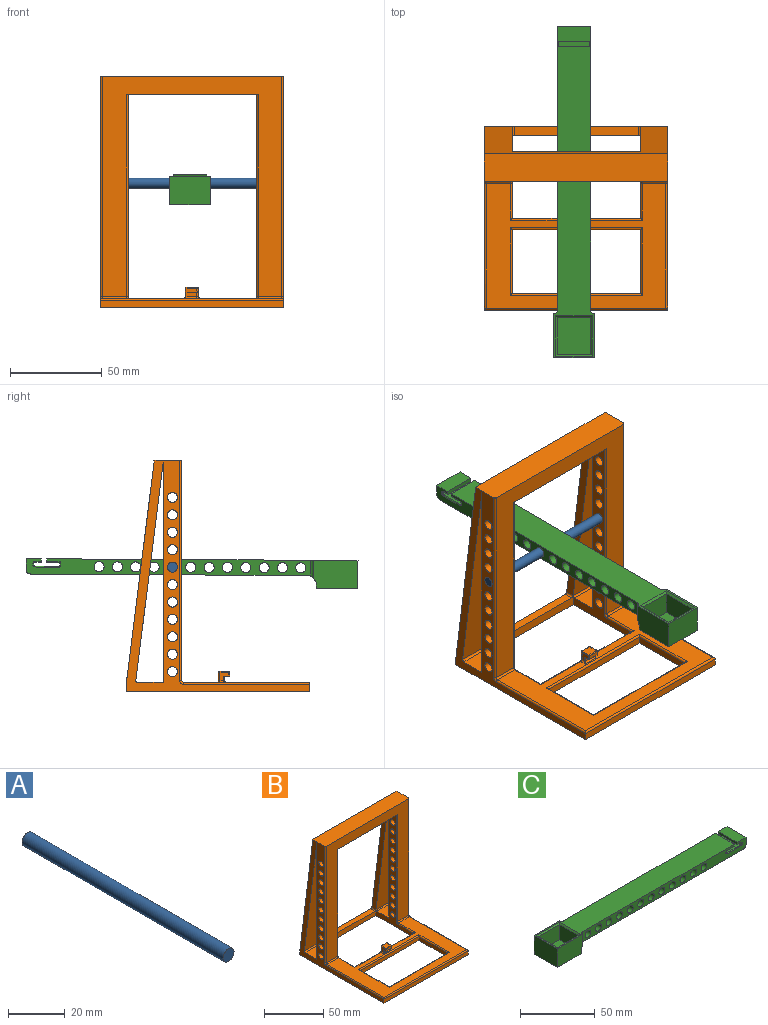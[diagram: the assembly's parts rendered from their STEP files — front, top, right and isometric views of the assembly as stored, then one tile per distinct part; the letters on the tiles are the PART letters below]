
ASSEMBLY  parts=3 mates=2
PART A: 3 faces, bbox 5.5x100x5.5 mm
  f0: cylinder r=2.75mm len=100mm, axis (0,1,0), area 1727.9mm2, adj f1,f2
  f1: plane 5.5x5.5mm, normal (0,-1,0), area 23.8mm2, adj f0
  f2: plane 5.5x5.5mm, normal (0,1,0), area 23.8mm2, adj f0
PART B: 108 faces, bbox 100.1x100.1x126.1 mm
  f0: plane 1.05x1.05mm, normal (0,-0.99,-0.12), area 0.2mm2, adj f25,f34,f106
  f1: plane 118.88x100mm, normal (0,-0.99,-0.12), area 4222.1mm2, adj f12,f13,f14,f22,f23,f24,f105,f107
  f2: plane 100x100mm, normal (0,0,-1), area 4421mm2, adj f7,f12,f13,f18,f19,f25,f27,f30
  f3: plane 98x67.9mm, normal (0,0,1), area 2547.8mm2, adj f60,f61,f67,f68,f70,f72,f73,f75
  f4: plane 14.67x13.96mm, normal (0,0,1), area 204.8mm2, adj f12,f14,f25,f107
  f5: plane 15.33x13.96mm, normal (0,0,1), area 214mm2, adj f13,f14,f27,f105
  f6: plane 68x5mm, normal (0,0,1), area 340mm2, adj f19,f34,f102,f106
  f7: plane 70x10.5mm, normal (0,1,0), area 316.6mm2, adj f2,f25,f27,f59,f60,f64,f74,f77
  f8: plane 5.87x5.25mm, normal (0,0,1), area 30.8mm2, adj f57,f92,f94,f95,f96
  f9: plane 5.87x2.16mm, normal (0,-1,0), area 12.6mm2, adj f58,f90,f92,f100
  f10: plane 6.34x3.14mm, normal (0,0,-1), area 17.7mm2, adj f11,f63,f98,f99,f100,f103
  f11: plane 5.87x2.32mm, normal (0,-1,0), area 13.6mm2, adj f10,f66,f72,f103
  f12: plane 126.06x100mm, normal (1,0,0), area 1863.8mm2, adj f1,f2,f4,f14,f17,f18,f19,f20
  f13: plane 126.06x100mm, normal (-1,0,0), area 1863.8mm2, adj f1,f2,f5,f14,f17,f18,f19,f20
  f14: plane 120x100mm, normal (0,1,0), area 4222.8mm2, adj f1,f4,f5,f12,f13,f25,f26,f27
  f15: plane 1.05x1.05mm, normal (0,-0.99,-0.12), area 0.2mm2, adj f27,f34,f102
  f16: plane 120.06x98mm, normal (0,-1,0), area 3838.7mm2, adj f21,f26,f62,f68,f69,f79,f83,f85
  f17: plane 120.05x100.05mm, normal (0,0.99,0.12), area 4256.6mm2, adj f12,f13,f19,f20,f22,f23,f24,f102
  f18: plane 100x4mm, normal (0,-1,0), area 400mm2, adj f2,f12,f13,f76
  f19: plane 100x5mm, normal (0,1,0), area 500mm2, adj f2,f6,f12,f13,f17
  f20: plane 100x1.06mm, normal (0,1,-0.06), area 106.3mm2, adj f12,f13,f17,f21
  f21: plane 100x15.06mm, normal (0,0,1), area 1505.7mm2, adj f12,f13,f16,f20,f69,f79
  f22: plane 110.1x18.85mm, normal (1,0,0), area 550.5mm2, adj f1,f17,f23,f27,f102
  f23: plane 70x5mm, normal (0,0,-1), area 350mm2, adj f1,f17,f22,f24
  f24: plane 110.1x18.85mm, normal (-1,0,0), area 550.5mm2, adj f1,f17,f23,f25,f106
  f25: plane 116.1x45mm, normal (-1,0,0), area 943.8mm2, adj f0,f2,f4,f7,f14,f24,f26,f34
  f26: plane 72x10mm, normal (0,0,-1), area 700.4mm2, adj f14,f16,f25,f27,f62,f85
  f27: plane 116.1x45mm, normal (1,0,0), area 943.8mm2, adj f2,f5,f7,f14,f15,f22,f26,f34
  f28: plane 4.25x4mm, normal (1,0,0), area 7.7mm2, adj f57,f58,f59,f63,f66,f67
  f29: plane 4.75x4.5mm, normal (-1,0,0), area 14.8mm2, adj f74,f75,f90,f94,f98,f103
  f30: plane 34.7x4mm, normal (-1,0,0), area 138.8mm2, adj f2,f31,f33,f87
  f31: plane 70x4mm, normal (0,-1,0), area 280mm2, adj f2,f30,f32,f89
  f32: plane 34.7x4mm, normal (1,0,0), area 138.8mm2, adj f2,f31,f33,f88
  f33: plane 70x4mm, normal (0,1,0), area 280mm2, adj f2,f30,f32,f86
  f34: plane 70x5mm, normal (0,-1,0), area 350mm2, adj f0,f2,f6,f15,f25,f27
  f35: cylinder r=2.75mm len=14.67mm, axis (-1,0,0), area 253.5mm2, adj f12,f25
  f36: cylinder r=2.75mm len=14.67mm, axis (-1,0,0), area 253.5mm2, adj f12,f25
  f37: cylinder r=2.75mm len=14.67mm, axis (-1,0,0), area 253.5mm2, adj f12,f25
  f38: cylinder r=2.75mm len=14.67mm, axis (-1,0,0), area 253.5mm2, adj f12,f25
  f39: cylinder r=2.75mm len=14.67mm, axis (-1,0,0), area 253.5mm2, adj f12,f25
  f40: cylinder r=2.75mm len=14.67mm, axis (-1,0,0), area 253.5mm2, adj f12,f25
  f41: cylinder r=2.75mm len=14.67mm, axis (-1,0,0), area 253.5mm2, adj f12,f25
  f42: cylinder r=2.75mm len=14.67mm, axis (-1,0,0), area 253.5mm2, adj f12,f25
  f43: cylinder r=2.75mm len=14.67mm, axis (-1,0,0), area 253.5mm2, adj f12,f25
  f44: cylinder r=2.75mm len=14.67mm, axis (-1,0,0), area 253.5mm2, adj f12,f25
  f45: cylinder r=2.75mm len=14.67mm, axis (-1,0,0), area 253.5mm2, adj f12,f25
  f46: cylinder r=2.75mm len=15.33mm, axis (1,0,0), area 264.8mm2, adj f13,f27
  f47: cylinder r=2.75mm len=15.33mm, axis (1,0,0), area 264.8mm2, adj f13,f27
  f48: cylinder r=2.75mm len=15.33mm, axis (1,0,0), area 264.8mm2, adj f13,f27
  f49: cylinder r=2.75mm len=15.33mm, axis (1,0,0), area 264.8mm2, adj f13,f27
  f50: cylinder r=2.75mm len=15.33mm, axis (1,0,0), area 264.8mm2, adj f13,f27
  f51: cylinder r=2.75mm len=15.33mm, axis (1,0,0), area 264.8mm2, adj f13,f27
  f52: cylinder r=2.75mm len=15.33mm, axis (1,0,0), area 264.8mm2, adj f13,f27
  f53: cylinder r=2.75mm len=15.33mm, axis (1,0,0), area 264.8mm2, adj f13,f27
  f54: cylinder r=2.75mm len=15.33mm, axis (1,0,0), area 264.8mm2, adj f13,f27
  f55: cylinder r=2.75mm len=15.33mm, axis (1,0,0), area 264.8mm2, adj f13,f27
  f56: cylinder r=2.75mm len=15.33mm, axis (1,0,0), area 264.8mm2, adj f13,f27
  f57: cylinder r=1mm len=5.25mm, axis (0,-1,0), area 7.7mm2, adj f8,f28,f91,f97
  f58: cylinder r=1mm len=2.16mm, axis (0,0,1), area 2.5mm2, adj f9,f28,f91,f101
  f59: cylinder r=1mm len=4.5mm, axis (0,0,1), area 6.8mm2, adj f7,f28,f64,f97
  f60: cylinder r=1mm len=31.73mm, axis (-1,0,0), area 48.8mm2, adj f3,f7,f61,f64
  f61: cylinder r=1mm len=19.9mm, axis (0,1,0), area 30.3mm2, adj f3,f25,f60,f65
  f62: cylinder r=1mm len=110.1mm, axis (0,0,-1), area 172.9mm2, adj f16,f25,f26,f65
  f63: cylinder r=1mm len=3.79mm, axis (0,-1,0), area 4.4mm2, adj f10,f28,f66,f101
  f64: torus R=2mm, axis (0,-1,0), area 3.4mm2, adj f7,f59,f60,f67
  f65: torus R=2mm, axis (-1,0,0), area 3.4mm2, adj f25,f61,f62,f68
  f66: cylinder r=1mm len=3.32mm, axis (0,0,1), area 4.2mm2, adj f11,f28,f63,f70
  f67: cylinder r=1mm len=1.44mm, axis (0,1,0), area 2.3mm2, adj f3,f28,f64,f70
  f68: cylinder r=1mm len=12.67mm, axis (-1,0,0), area 19.9mm2, adj f3,f16,f65,f71
  f69: cylinder r=1mm len=120.06mm, axis (0,0,1), area 188.6mm2, adj f12,f16,f21,f71
  f70: torus R=2mm, axis (0,0,-1), area 3.4mm2, adj f3,f66,f67,f72
  f71: torus R=2mm, axis (1,0,0), area 3.4mm2, adj f12,f68,f69,f73
  f72: cylinder r=1mm len=7.37mm, axis (1,0,0), area 10.1mm2, adj f3,f11,f70,f104
  f73: cylinder r=1mm len=68.9mm, axis (0,-1,0), area 107.7mm2, adj f3,f12,f71,f76
  f74: cylinder r=1mm len=4.5mm, axis (0,0,-1), area 7.1mm2, adj f7,f29,f77,f95
  f75: cylinder r=1mm len=3.44mm, axis (0,-1,0), area 3.9mm2, adj f3,f29,f77,f104
  f76: cylinder r=1mm len=100mm, axis (1,0,0), area 155.9mm2, adj f3,f18,f73,f78
  f77: torus R=2mm, axis (0,-1,0), area 3.4mm2, adj f7,f74,f75,f80
  f78: cylinder r=1mm len=68.9mm, axis (0,1,0), area 107.7mm2, adj f3,f13,f76,f81
  f79: cylinder r=1mm len=120.06mm, axis (0,0,-1), area 188.6mm2, adj f13,f16,f21,f81
  f80: cylinder r=1mm len=30.9mm, axis (-1,0,0), area 47.5mm2, adj f3,f7,f77,f82
  f81: torus R=2mm, axis (1,0,0), area 3.4mm2, adj f13,f78,f79,f83
  f82: cylinder r=1mm len=19.9mm, axis (0,-1,0), area 30.3mm2, adj f3,f27,f80,f84
  f83: cylinder r=1mm len=13.33mm, axis (-1,0,0), area 20.9mm2, adj f3,f16,f81,f84
  f84: torus R=2mm, axis (-1,0,0), area 3.4mm2, adj f27,f82,f83,f85
  f85: cylinder r=1mm len=110.1mm, axis (0,0,1), area 172.9mm2, adj f16,f26,f27,f84
  f86: cylinder r=1mm len=72mm, axis (1,0,0), area 111.1mm2, adj f3,f33,f87,f88
  f87: cylinder r=1mm len=36.7mm, axis (0,1,0), area 55.6mm2, adj f3,f30,f86,f89
  f88: cylinder r=1mm len=36.7mm, axis (0,-1,0), area 55.6mm2, adj f3,f32,f86,f89
  f89: cylinder r=1mm len=72mm, axis (-1,0,0), area 111.1mm2, adj f3,f31,f87,f88
  f90: cylinder r=0.5mm len=2.16mm, axis (0,0,-1), area 1.7mm2, adj f9,f29,f93,f99
  f91: bspline ~1.19x1mm, area 0.8mm2, adj f57,f58,f92
  f92: cylinder r=0.5mm len=5.87mm, axis (-1,0,0), area 4.6mm2, adj f8,f9,f91,f93
  f93: sphere r=0.5mm, area 0.4mm2, adj f90,f92,f94
  f94: cylinder r=0.5mm len=4.75mm, axis (0,1,0), area 3.7mm2, adj f8,f29,f93,f95
  f95: torus R=0.5mm, axis (0,0,-1), area 1mm2, adj f8,f74,f94,f96
  f96: cylinder r=0.5mm len=5.37mm, axis (-1,0,0), area 4.2mm2, adj f7,f8,f95,f97
  f97: bspline ~1.19x1mm, area 0.8mm2, adj f57,f59,f96
  f98: cylinder r=0.02mm len=2.81mm, axis (0,1,0), area 0.1mm2, adj f10,f29,f99,f103
  f99: torus R=0.48mm, axis (0,0,1), area 0mm2, adj f10,f90,f98,f100
  f100: cylinder r=0.02mm len=5.87mm, axis (-1,0,0), area 0.2mm2, adj f9,f10,f99,f101
  f101: bspline ~1.13x1mm, area 0mm2, adj f58,f63,f100
  f102: cylinder r=1mm len=5.13mm, axis (0,1,0), area 7.9mm2, adj f6,f15,f17,f22
  f103: cylinder r=0.5mm len=2.34mm, axis (0,0,-1), area 1.8mm2, adj f10,f11,f29,f98,f104
  f104: bspline ~1.5x1.5mm, area 0.9mm2, adj f72,f75,f103
  f105: cylinder r=1mm len=15.33mm, axis (-1,0,0), area 26mm2, adj f1,f5,f13,f27
  f106: cylinder r=1mm len=5.13mm, axis (0,-1,0), area 7.9mm2, adj f0,f6,f17,f24
  f107: cylinder r=1mm len=14.67mm, axis (-1,0,0), area 24.9mm2, adj f1,f4,f12,f25
PART C: 65 faces, bbox 181x22x15.4 mm
  f0: plane 169.8x22mm, normal (0,0,1), area 2714.5mm2, adj f11,f12,f13,f14,f22,f23,f59,f60
  f1: plane 18x8.27mm, normal (0,0,1), area 148.9mm2, adj f4,f5,f22,f23
  f2: plane 150.77x18mm, normal (0,0,-1), area 2713.9mm2, adj f3,f22,f23,f58
  f3: cylinder r=2.5mm len=18mm, axis (0,1,0), area 70.7mm2, adj f2,f4,f22,f23
  f4: plane 18x5.85mm, normal (1,0,0), area 105.3mm2, adj f1,f3,f22,f23
  f5: plane 18x2mm, normal (-1,0,0), area 35.9mm2, adj f1,f6,f22,f23,f49,f57
  f6: plane 17x3.5mm, normal (0,0,-1), area 59.5mm2, adj f5,f49,f54,f57
  f7: plane 17x1mm, normal (-1,0,0), area 17mm2, adj f50,f51,f54,f55
  f8: plane 17x13.21mm, normal (0,0,1), area 224.5mm2, adj f36,f38,f39,f51
  f9: plane 17x1mm, normal (1,0,0), area 17mm2, adj f39,f40,f44,f45
  f10: plane 17x6.81mm, normal (0,0,-1), area 115.7mm2, adj f11,f41,f45,f47
  f11: plane 18x2mm, normal (1,0,0), area 35.9mm2, adj f0,f10,f22,f23,f41,f47
  f12: plane 24.08x15.35mm, normal (0,-1,0), area 363.6mm2, adj f0,f14,f15,f16,f58,f63
  f13: plane 24.08x15.35mm, normal (0,1,0), area 363.6mm2, adj f0,f14,f15,f16,f58,f64
  f14: plane 22x15.35mm, normal (-1,0,0), area 337.7mm2, adj f0,f12,f13,f15
  f15: plane 22.7x22mm, normal (0,0,-1), area 499.5mm2, adj f12,f13,f14,f16
  f16: plane 22x2mm, normal (1,0,0), area 44mm2, adj f12,f13,f15,f58
  f17: plane 18x12.4mm, normal (1,0,0), area 223.2mm2, adj f18,f20,f21,f61
  f18: plane 20x12.4mm, normal (0,1,0), area 248mm2, adj f17,f19,f21,f62
  f19: plane 18x12.4mm, normal (-1,0,0), area 223.2mm2, adj f18,f20,f21,f60
  f20: plane 20x12.4mm, normal (0,-1,0), area 248mm2, adj f17,f19,f21,f59
  f21: plane 20x18mm, normal (0,0,1), area 360mm2, adj f17,f18,f19,f20
  f22: plane 154.9x8.62mm, normal (0,-1,0), area 958.1mm2, adj f0,f1,f2,f3,f4,f5,f11,f24
  f23: plane 154.9x8.62mm, normal (0,1,0), area 958.1mm2, adj f0,f1,f2,f3,f4,f5,f11,f24
  f24: cylinder r=2.75mm len=18mm, axis (0,1,0), area 311mm2, adj f22,f23
  f25: cylinder r=2.75mm len=18mm, axis (0,1,0), area 311mm2, adj f22,f23
  f26: cylinder r=2.75mm len=18mm, axis (0,1,0), area 311mm2, adj f22,f23
  f27: cylinder r=2.75mm len=18mm, axis (0,1,0), area 311mm2, adj f22,f23
  f28: cylinder r=2.75mm len=18mm, axis (0,1,0), area 311mm2, adj f22,f23
  f29: cylinder r=2.75mm len=18mm, axis (0,1,0), area 311mm2, adj f22,f23
  f30: cylinder r=2.75mm len=18mm, axis (0,1,0), area 311mm2, adj f22,f23
  f31: cylinder r=2.75mm len=18mm, axis (0,1,0), area 311mm2, adj f22,f23
  f32: cylinder r=2.75mm len=18mm, axis (0,1,0), area 311mm2, adj f22,f23
  f33: cylinder r=2.75mm len=18mm, axis (0,1,0), area 311mm2, adj f22,f23
  f34: cylinder r=2.75mm len=18mm, axis (0,1,0), area 311mm2, adj f22,f23
  f35: cylinder r=2.75mm len=18mm, axis (0,1,0), area 311mm2, adj f22,f23
  f36: cylinder r=0.5mm len=13.21mm, axis (1,0,0), area 10.4mm2, adj f8,f22,f37,f48
  f37: torus R=1mm, axis (0,-1,0), area 0.8mm2, adj f22,f36,f39,f40
  f38: cylinder r=0.5mm len=13.21mm, axis (-1,0,0), area 10.4mm2, adj f8,f23,f42,f53
  f39: cylinder r=0.5mm len=17mm, axis (0,-1,0), area 13.4mm2, adj f8,f9,f37,f42
  f40: cylinder r=0.5mm len=1mm, axis (0,0,-1), area 0.8mm2, adj f9,f22,f37,f43
  f41: cylinder r=0.5mm len=6.81mm, axis (-1,0,0), area 5.3mm2, adj f10,f11,f22,f43
  f42: torus R=1mm, axis (0,-1,0), area 0.8mm2, adj f23,f38,f39,f44
  f43: torus R=1mm, axis (0,-1,0), area 0.8mm2, adj f22,f40,f41,f45
  f44: cylinder r=0.5mm len=1mm, axis (0,0,1), area 0.8mm2, adj f9,f23,f42,f46
  f45: cylinder r=0.5mm len=17mm, axis (0,-1,0), area 13.4mm2, adj f9,f10,f43,f46
  f46: torus R=1mm, axis (0,-1,0), area 0.8mm2, adj f23,f44,f45,f47
  f47: cylinder r=0.5mm len=6.81mm, axis (1,0,0), area 5.3mm2, adj f10,f11,f23,f46
  f48: torus R=1mm, axis (0,-1,0), area 0.8mm2, adj f22,f36,f50,f51
  f49: cylinder r=0.5mm len=3.5mm, axis (-1,0,0), area 2.7mm2, adj f5,f6,f22,f52
  f50: cylinder r=0.5mm len=1mm, axis (0,0,1), area 0.8mm2, adj f7,f22,f48,f52
  f51: cylinder r=0.5mm len=17mm, axis (0,1,0), area 13.4mm2, adj f7,f8,f48,f53
  f52: torus R=1mm, axis (0,-1,0), area 0.8mm2, adj f22,f49,f50,f54
  f53: torus R=1mm, axis (0,-1,0), area 0.8mm2, adj f23,f38,f51,f55
  f54: cylinder r=0.5mm len=17mm, axis (0,-1,0), area 13.4mm2, adj f6,f7,f52,f56
  f55: cylinder r=0.5mm len=1mm, axis (0,0,-1), area 0.8mm2, adj f7,f23,f53,f56
  f56: torus R=1mm, axis (0,-1,0), area 0.8mm2, adj f23,f54,f55,f57
  f57: cylinder r=0.5mm len=3.5mm, axis (1,0,0), area 2.7mm2, adj f5,f6,f23,f56
  f58: cylinder r=5mm len=22mm, axis (0,1,0), area 158.8mm2, adj f2,f12,f13,f16,f22,f23,f63,f64
  f59: plane 22x1mm, normal (0,-0.71,0.71), area 29.7mm2, adj f0,f20,f60,f61
  f60: plane 20x1mm, normal (-0.71,0,0.71), area 26.9mm2, adj f0,f19,f59,f62
  f61: plane 20x1mm, normal (0.71,0,0.71), area 26.9mm2, adj f0,f17,f59,f62
  f62: plane 22x1mm, normal (0,0.71,0.71), area 29.7mm2, adj f0,f18,f60,f61
  f63: cylinder r=2mm len=9.91mm, axis (0,0,1), area 29.4mm2, adj f0,f12,f22,f58
  f64: cylinder r=2mm len=9.91mm, axis (0,0,-1), area 29.4mm2, adj f0,f13,f23,f58
PLACE A rot(axis=(0,0,-1),90deg) t=(167.66,-5.83,-146.84)mm
PLACE B t=(67.66,10.78,-180.6)mm
PLACE C rot(axis=(0,0,1),90deg) t=(105.57,1.94,-139.84)mm
MATE cylindrical A.f0 <-> B.f42  axis (1,0,0) through (167.66,11.26,-126.96)mm
MATE cylindrical C.f29 <-> A.f0  axis (-1,0,0) through (107.57,11.26,-126.96)mm
